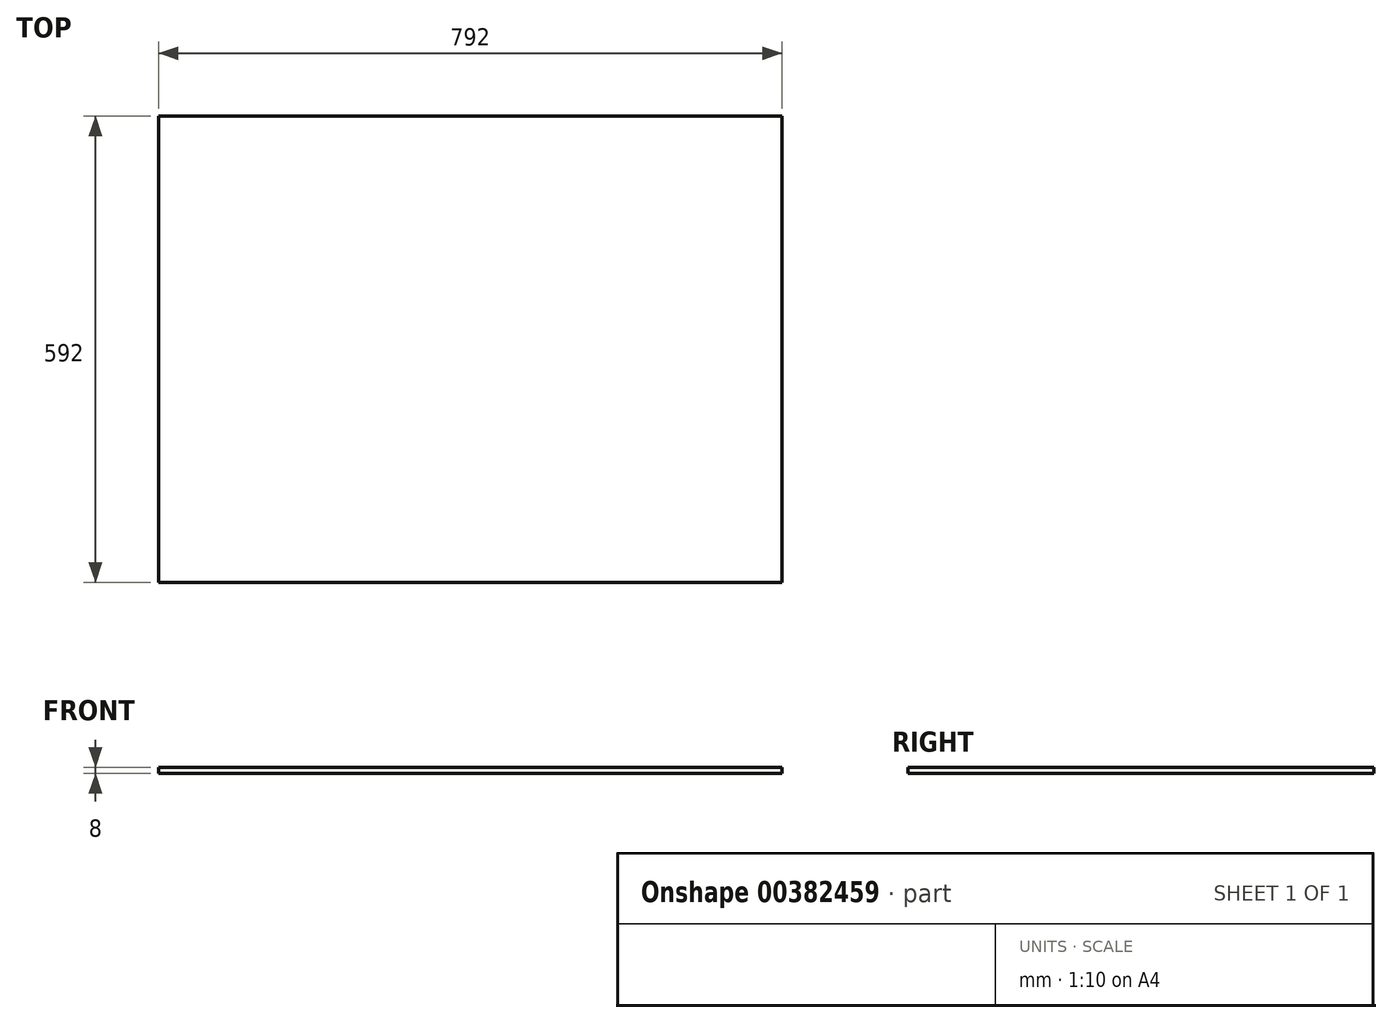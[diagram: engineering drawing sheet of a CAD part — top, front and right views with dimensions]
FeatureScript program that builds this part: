
annotation { "Feature Type Name" : "Feature", "Feature Type Description" : "" }
export const myFeature = defineFeature(function(context is Context, id is Id, definition is map)
    precondition{}
    {
        {
            var Q0;
            Q0=qCreatedBy(makeId("Top.planeOp"),FACE);
            var sketch = newSketch(context, id + "F0", { "sketchPlane" : qUnion([Q0])});
            skLineSegment(sketch, "E0.bottom", {"start": v(-396, 296) * mm, "end": v(396, 296) * mm});
            skLineSegment(sketch, "E0.top", {"start": v(-396, -296) * mm, "end": v(396, -296) * mm});
            skLineSegment(sketch, "E0.left", {"start": v(-396, 296) * mm, "end": v(-396, -296) * mm});
            skLineSegment(sketch, "E0.right", {"start": v(396, 296) * mm, "end": v(396, -296) * mm});
            skPoint(sketch, "E0.middle", {"position": v(0, 0) * mm});
            skSolve(sketch);
        }
        {
            var Q0;
            Q0=makeQuery(id+"F0.imprint","IMPRINT",FACE,{"disambiguationData":[TD([[makeQuery(id+"F0.imprint","IMPRINT",EDGE,{"derivedFrom":sQuery(id+"F0.wireOp",EDGE,"E0.bottom")}),-1.0]])]});
            extrude(context, id + "F1", {"entities" : qUnion([Q0]), "endBound" : BoundingType.SYMMETRIC, "depth" : 8 * mm});
        }
    });
